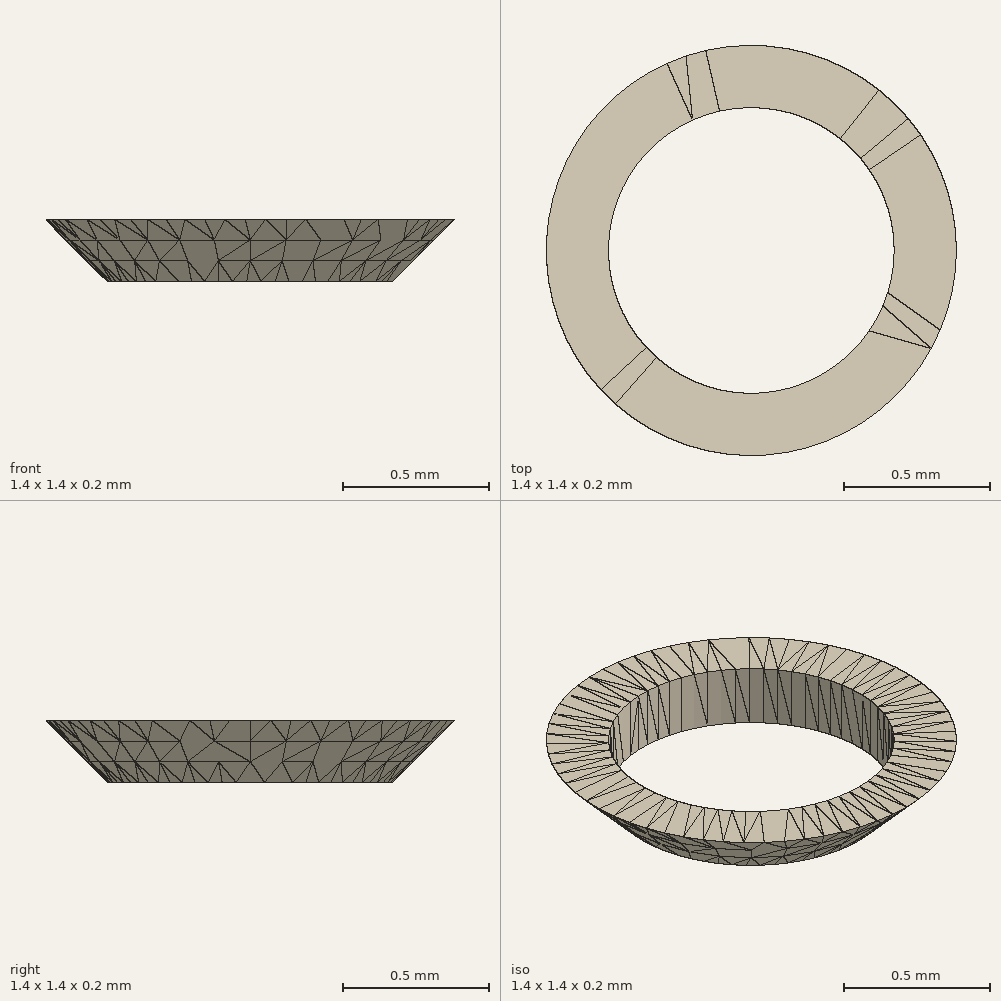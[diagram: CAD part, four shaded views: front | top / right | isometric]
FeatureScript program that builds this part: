
annotation { "Feature Type Name" : "Feature", "Feature Type Description" : "" }
export const myFeature = defineFeature(function(context is Context, id is Id, definition is map)
    precondition{}
    {
        {
            var Q0;
            Q0=qCreatedBy(makeId("Top.planeOp"),FACE);
            var sketch = newSketch(context, id + "F0", { "sketchPlane" : qUnion([Q0])});
            skCircle(sketch, "E0", {"center": v(0, 0) * mm, "radius": 0.7 * mm});
            skCircle(sketch, "E1", {"center": v(0, 0) * mm, "radius": 0.5 * mm});
            skSolve(sketch);
        }
        {
            var Q0;
            Q0=makeQuery(id+"F0.imprint","IMPRINT",FACE,{"disambiguationData":[TD([[makeQuery(id+"F0.imprint","IMPRINT",EDGE,{"derivedFrom":sQuery(id+"F0.wireOp",EDGE,"E0")}),1.0]])]});
            extrude(context, id + "F1", {"entities" : qUnion([Q0]), "depth" : .3 * mm, "offsetDistance" : 25 * mm});
        }
        {
            var Q0;
            Q0=makeQuery(id+"F1.opExtrude","CAP_EDGE",EDGE,{"disambiguationData":[OSD([sQuery(id+"F0.wireOp",EDGE,"E0")])],"isStart":true});
            chamfer(context, id + "F2", {"entities" : qUnion([Q0]), "width" : .3 * mm, "tangentPropagation" : true});
        }
    });
